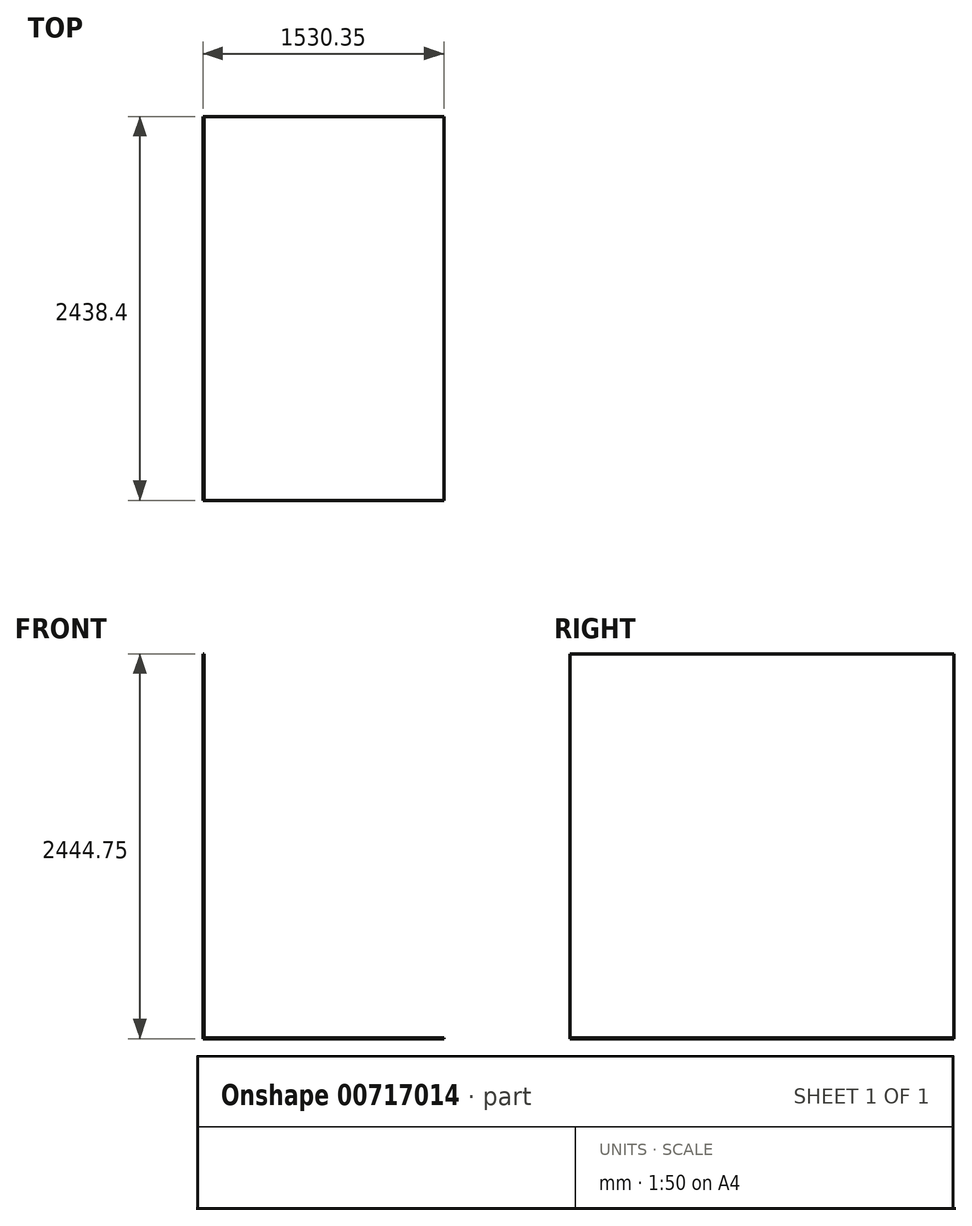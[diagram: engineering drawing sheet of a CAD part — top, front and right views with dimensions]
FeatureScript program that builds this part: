
annotation { "Feature Type Name" : "Feature", "Feature Type Description" : "" }
export const myFeature = defineFeature(function(context is Context, id is Id, definition is map)
    precondition{}
    {
        {
            var Q0;
            Q0=qCreatedBy(makeId("Front.planeOp"),FACE);
            var sketch = newSketch(context, id + "F0", { "sketchPlane" : qUnion([Q0])});
            skLineSegment(sketch, "E0", {"start": v(0, 0) * mm, "end": v(0, 2444.75) * mm});
            skLineSegment(sketch, "E1", {"start": v(0, 0) * mm, "end": v(1530.35, 0) * mm});
            skLineSegment(sketch, "E2.0", {"start": v(6.35, 6.35) * mm, "end": v(6.35, 2444.75) * mm});
            skLineSegment(sketch, "E2.1", {"start": v(6.35, 6.35) * mm, "end": v(1530.35, 6.35) * mm});
            skLineSegment(sketch, "E3", {"start": v(0, 2444.75) * mm, "end": v(6.35, 2444.75) * mm});
            skLineSegment(sketch, "E4", {"start": v(1530.35, 6.35) * mm, "end": v(1530.35, 0) * mm});
            skSolve(sketch);
        }
        {
            var Q0;
            Q0=makeQuery(id+"F0.imprint","IMPRINT",FACE,{"disambiguationData":[TD([[makeQuery(id+"F0.imprint","IMPRINT",EDGE,{"derivedFrom":sQuery(id+"F0.wireOp",EDGE,"E0")}),-1.0]])]});
            extrude(context, id + "F1", {"entities" : qUnion([Q0]), "depth" : 2438.4 * mm, "offsetDistance" : 25.4 * mm});
        }
    });
